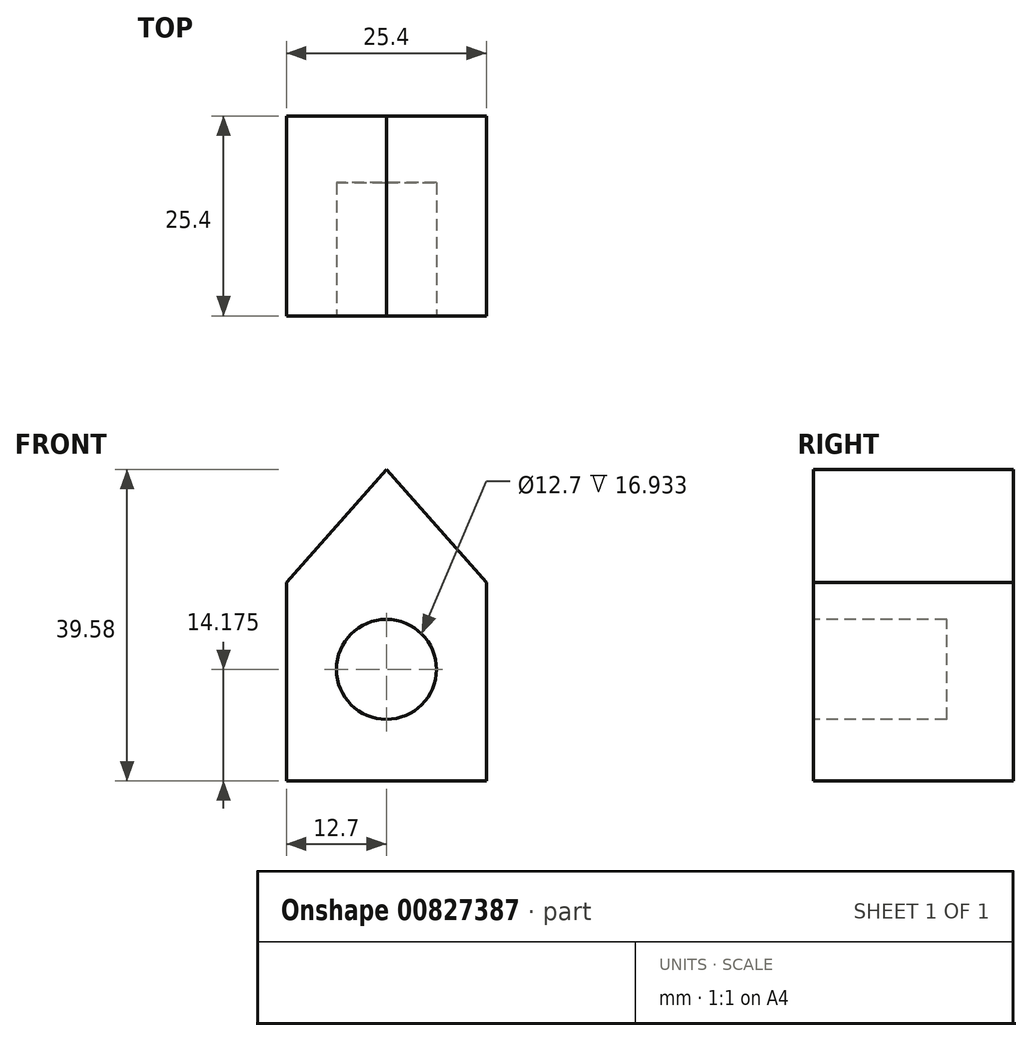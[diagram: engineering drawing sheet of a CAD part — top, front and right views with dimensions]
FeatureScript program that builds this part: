
annotation { "Feature Type Name" : "Feature", "Feature Type Description" : "" }
export const myFeature = defineFeature(function(context is Context, id is Id, definition is map)
    precondition{}
    {
        {
            assignVariable(context, id + "F0", {"name" : "x", "anyValue" : 25.4 * mm});
        }
        {
            var Q0;
            Q0=qCreatedBy(makeId("Front.planeOp"),FACE);
            var sketch = newSketch(context, id + "F1", { "sketchPlane" : qUnion([Q0])});
            skLineSegment(sketch, "E0.bottom", {"start": v(0, 0) * mm, "end": v(25.4, 0) * mm});
            skLineSegment(sketch, "E0.top", {"start": v(0, 25.23) * mm, "end": v(25.4, 25.23) * mm});
            skLineSegment(sketch, "E0.left", {"start": v(0, 0) * mm, "end": v(0, 25.23) * mm});
            skLineSegment(sketch, "E0.right", {"start": v(25.4, 0) * mm, "end": v(25.4, 25.23) * mm});
            skLineSegment(sketch, "E1", {"start": v(0, 25.23) * mm, "end": v(12.7, 39.58) * mm});
            skLineSegment(sketch, "E2", {"start": v(12.7, 39.58) * mm, "end": v(25.4, 25.23) * mm});
            skSolve(sketch);
        }
        {
            var Q0;
            Q0=makeQuery(id+"F1.imprint","IMPRINT",FACE,{"disambiguationData":[TD([[makeQuery(id+"F1.imprint","IMPRINT",EDGE,{"derivedFrom":sQuery(id+"F1.wireOp",EDGE,"E0.top")}),1.0]])]});
            var Q1;
            Q1=makeQuery(id+"F1.imprint","IMPRINT",FACE,{"disambiguationData":[TD([[makeQuery(id+"F1.imprint","IMPRINT",EDGE,{"derivedFrom":sQuery(id+"F1.wireOp",EDGE,"E0.bottom")}),1.0]])]});
            extrude(context, id + "F2", {"entities" : qUnion([Q0, Q1]), "oppositeDirection" : true, "depth" : getVariable(context, 'x'), "offsetDistance" : 25.4 * mm});
        }
        {
            var Q0;
            Q0=makeQuery(id+"F2.opExtrude","CAP_FACE",FACE,{"disambiguationData":[OSD([sQuery(id+"F1.wireOp",EDGE,"E0.bottom"),sQuery(id+"F1.wireOp",EDGE,"E0.left"),sQuery(id+"F1.wireOp",EDGE,"E0.right"),sQuery(id+"F1.wireOp",EDGE,"E1"),sQuery(id+"F1.wireOp",EDGE,"E2")])],"isStart":true});
            var sketch = newSketch(context, id + "F3", { "sketchPlane" : qUnion([Q0])});
            skCircle(sketch, "E3", {"center": v(12.7, 14.18) * mm, "radius": 6.35 * mm});
            skCircle(sketch, "E4", {"center": v(12.7, 3.7) * mm, "radius": 1.59 * mm});
            skSolve(sketch);
        }
        {
            var Q0;
            Q0=makeQuery(id+"F3.imprint","IMPRINT",FACE,{"disambiguationData":[TD([[makeQuery(id+"F3.imprint","IMPRINT",EDGE,{"derivedFrom":sQuery(id+"F3.wireOp",EDGE,"E3")}),1.0]])]});
            extrude(context, id + "F4", {"entities" : qUnion([Q0]), "operationType" : NewBodyOperationType.REMOVE, "oppositeDirection" : true, "depth" : getVariable(context, 'x') / 1.5, "offsetDistance" : 25.4 * mm});
        }
        {
            var Q0;
            Q0=sQuery(id+"F3.wireOp",EDGE,"E4");
            extrude(context, id + "F5", {"bodyType" : ToolBodyType.SURFACE, "surfaceEntities" : qUnion([Q0]), "depth" : getVariable(context, 'x') / 4, "offsetDistance" : 25.4 * mm});
        }
    });
